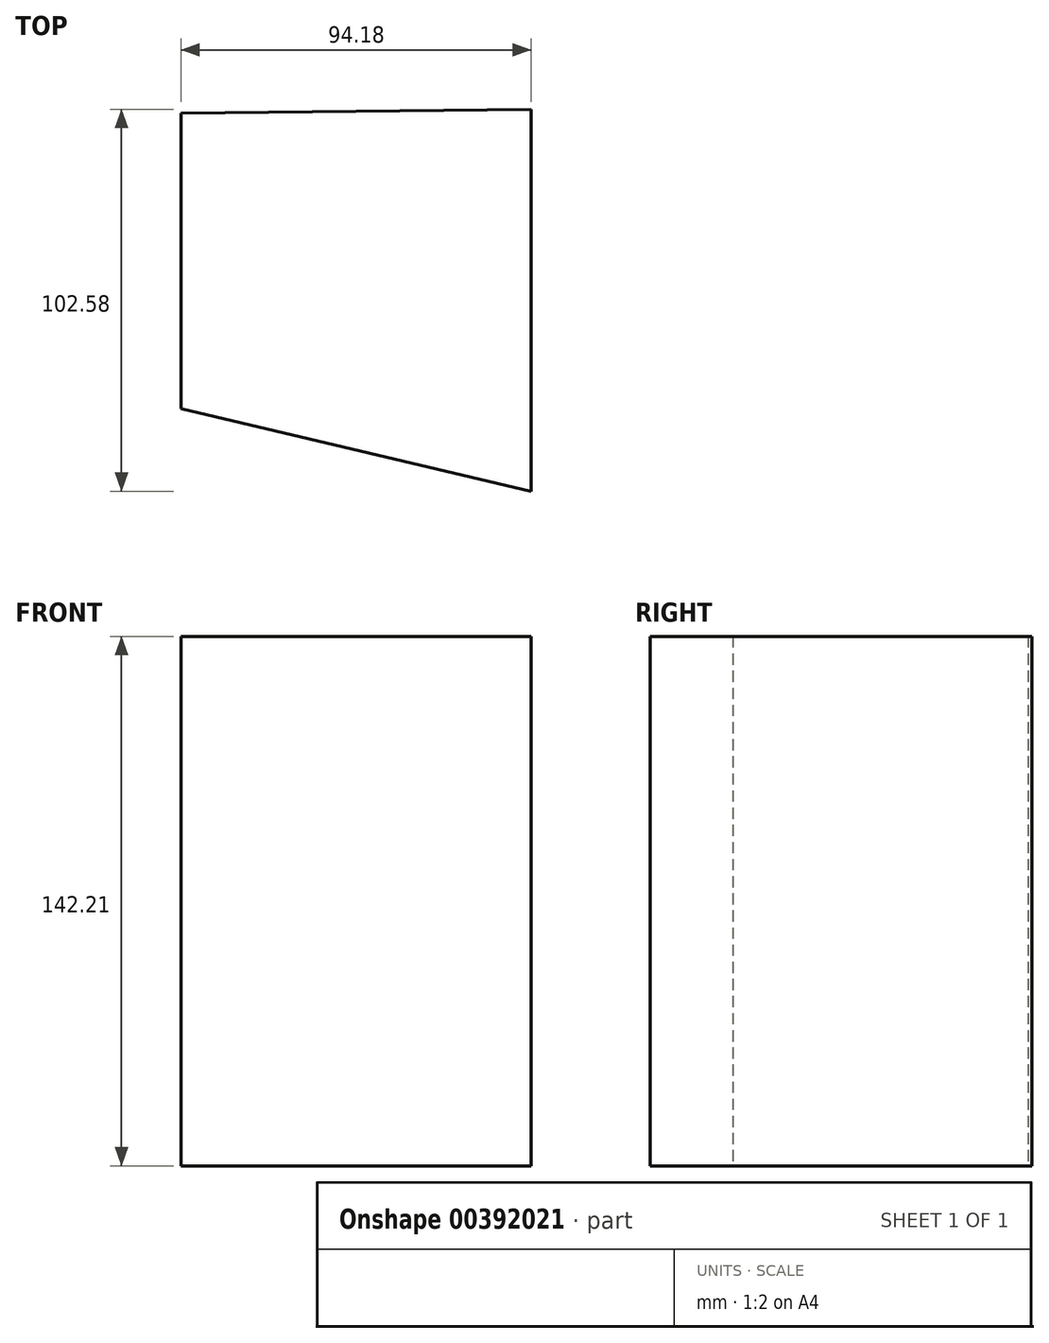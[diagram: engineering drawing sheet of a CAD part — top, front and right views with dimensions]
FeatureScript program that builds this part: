
annotation { "Feature Type Name" : "Feature", "Feature Type Description" : "" }
export const myFeature = defineFeature(function(context is Context, id is Id, definition is map)
    precondition{}
    {
        {
            var Q0;
            Q0=qCreatedBy(makeId("Top.planeOp"),FACE);
            var sketch = newSketch(context, id + "F0", { "sketchPlane" : qUnion([Q0])});
            skLineSegment(sketch, "E0", {"start": v(-53.4, 43.2) * mm, "end": v(-53.4, -36.15) * mm});
            skLineSegment(sketch, "E1", {"start": v(-53.4, -36.15) * mm, "end": v(40.8, -58.34) * mm});
            skLineSegment(sketch, "E2", {"start": v(40.8, -58.34) * mm, "end": v(40.8, 44.24) * mm});
            skLineSegment(sketch, "E3", {"start": v(40.8, 44.24) * mm, "end": v(-53.4, 43.2) * mm});
            skLineSegment(sketch, "E4", {"start": v(-6.3, 43.72) * mm, "end": v(-12.45, 62.54) * mm, "construction": true});
            skSolve(sketch);
        }
        {
            var Q0;
            Q0=makeQuery(id+"F0.imprint","IMPRINT",FACE,{"disambiguationData":[TD([[makeQuery(id+"F0.imprint","IMPRINT",EDGE,{"derivedFrom":sQuery(id+"F0.wireOp",EDGE,"E0")}),1.0]])]});
            extrude(context, id + "F1", {"entities" : qUnion([Q0]), "depth" : 142.2 * mm});
        }
    });
